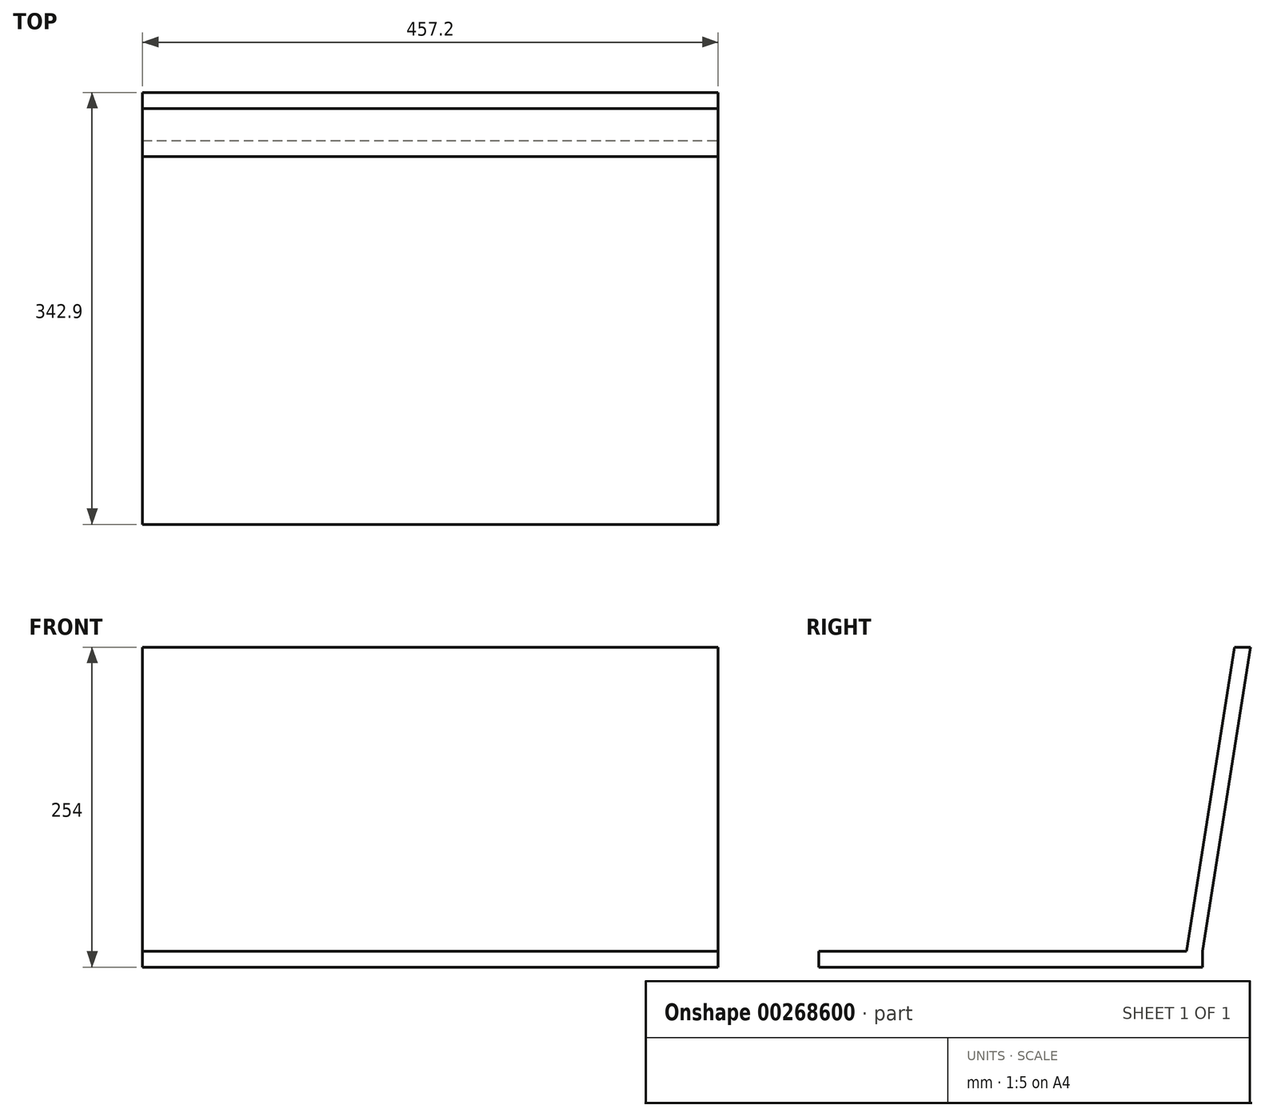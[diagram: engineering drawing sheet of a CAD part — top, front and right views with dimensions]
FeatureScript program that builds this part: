
annotation { "Feature Type Name" : "Feature", "Feature Type Description" : "" }
export const myFeature = defineFeature(function(context is Context, id is Id, definition is map)
    precondition{}
    {
        {
            var Q0;
            Q0=qCreatedBy(makeId("Top.planeOp"),FACE);
            var sketch = newSketch(context, id + "F0", { "sketchPlane" : qUnion([Q0])});
            skLineSegment(sketch, "E0.bottom", {"start": v(-228.6, 152.4) * mm, "end": v(228.6, 152.4) * mm});
            skLineSegment(sketch, "E0.top", {"start": v(-228.6, -152.4) * mm, "end": v(228.6, -152.4) * mm});
            skLineSegment(sketch, "E0.left", {"start": v(-228.6, 152.4) * mm, "end": v(-228.6, -152.4) * mm});
            skLineSegment(sketch, "E0.right", {"start": v(228.6, 152.4) * mm, "end": v(228.6, -152.4) * mm});
            skSolve(sketch);
        }
        {
            var Q0;
            Q0=makeQuery(id+"F0.imprint","IMPRINT",FACE,{"disambiguationData":[TD([[makeQuery(id+"F0.imprint","IMPRINT",EDGE,{"derivedFrom":sQuery(id+"F0.wireOp",EDGE,"E0.bottom")}),-1.0]])]});
            extrude(context, id + "F1", {"entities" : qUnion([Q0]), "depth" : 12.7 * mm, "offsetDistance" : 25.4 * mm});
        }
        {
            var Q0;
            Q0=makeQuery(id+"F1.opExtrude","CAP_FACE",FACE,{"disambiguationData":[OSD([sQuery(id+"F0.wireOp",EDGE,"E0.bottom"),sQuery(id+"F0.wireOp",EDGE,"E0.top"),sQuery(id+"F0.wireOp",EDGE,"E0.left"),sQuery(id+"F0.wireOp",EDGE,"E0.right")])],"isStart":false});
            var sketch = newSketch(context, id + "F2", { "sketchPlane" : qUnion([Q0])});
            skLineSegment(sketch, "E1.bottom", {"start": v(-228.6, 152.4) * mm, "end": v(228.6, 152.4) * mm});
            skLineSegment(sketch, "E1.top", {"start": v(-228.6, 139.7) * mm, "end": v(228.6, 139.7) * mm});
            skLineSegment(sketch, "E1.left", {"start": v(-228.6, 152.4) * mm, "end": v(-228.6, 139.7) * mm});
            skLineSegment(sketch, "E1.right", {"start": v(228.6, 152.4) * mm, "end": v(228.6, 139.7) * mm});
            skSolve(sketch);
        }
        {
            var Q0;
            Q0=qCreatedBy(makeId("Top.planeOp"),FACE);
            cPlane(context, id + "F3", {"entities" : qUnion([Q0]), "cplaneType" : CPlaneType.OFFSET, "offset" : 254 * mm, "width" : 152.4 * mm, "height" : 152.4 * mm});
        }
        {
            var Q0;
            Q0=qCreatedBy(id+"F3.planeOp",FACE);
            var sketch = newSketch(context, id + "F4", { "sketchPlane" : qUnion([Q0])});
            skLineSegment(sketch, "E2.bottom", {"start": v(-228.6, 190.5) * mm, "end": v(228.6, 190.5) * mm});
            skLineSegment(sketch, "E2.top", {"start": v(-228.6, 177.8) * mm, "end": v(228.6, 177.8) * mm});
            skLineSegment(sketch, "E2.left", {"start": v(-228.6, 190.5) * mm, "end": v(-228.6, 177.8) * mm});
            skLineSegment(sketch, "E2.right", {"start": v(228.6, 190.5) * mm, "end": v(228.6, 177.8) * mm});
            skSolve(sketch);
        }
        {
            var Q0;
            Q0=makeQuery(id+"F2.imprint","IMPRINT",FACE,{"disambiguationData":[TD([[makeQuery(id+"F2.imprint","IMPRINT",EDGE,{"derivedFrom":sQuery(id+"F2.wireOp",EDGE,"E1.bottom")}),-1.0]])]});
            var Q1;
            Q1=makeQuery(id+"F4.imprint","IMPRINT",FACE,{"disambiguationData":[TD([[makeQuery(id+"F4.imprint","IMPRINT",EDGE,{"derivedFrom":sQuery(id+"F4.wireOp",EDGE,"E2.bottom")}),-1.0]])]});
            loft(context, id + "F5", {"operationType" : NewBodyOperationType.ADD, "sheetProfilesArray" : [{ "sheetProfileEntities" : qUnion([Q0]) }, { "sheetProfileEntities" : qUnion([Q1]) }]});
        }
    });
